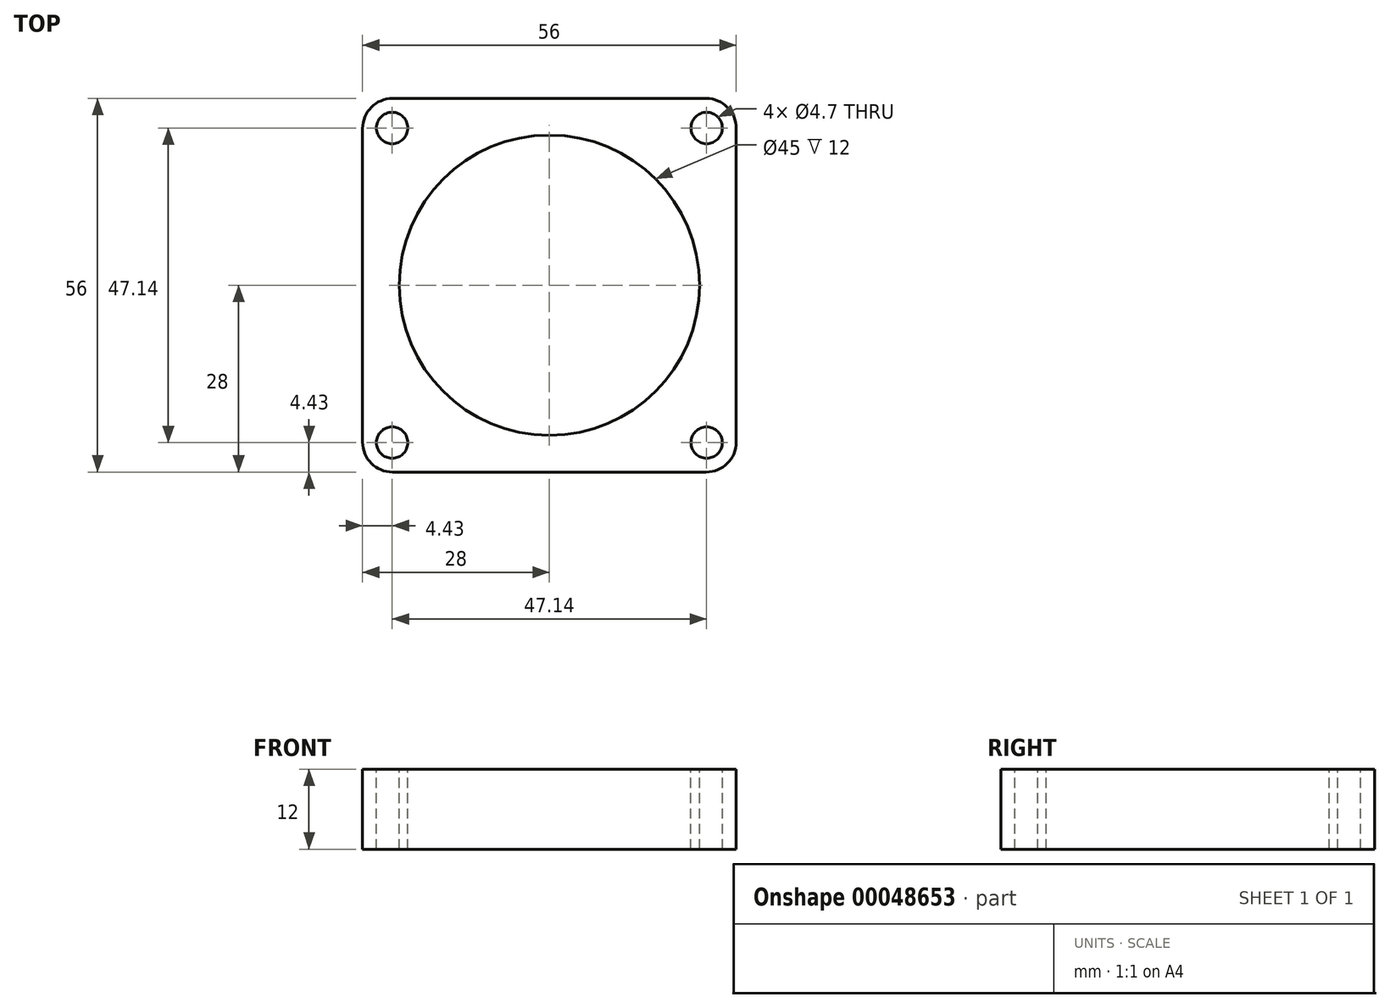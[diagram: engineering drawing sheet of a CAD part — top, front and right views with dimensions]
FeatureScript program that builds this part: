
annotation { "Feature Type Name" : "Feature", "Feature Type Description" : "" }
export const myFeature = defineFeature(function(context is Context, id is Id, definition is map)
    precondition{}
    {
        {
            var Q0;
            Q0=qCreatedBy(makeId("Top.planeOp"),FACE);
            var sketch = newSketch(context, id + "F0", { "sketchPlane" : qUnion([Q0])});
            skLineSegment(sketch, "E0.bottom", {"start": v(0, 0) * mm, "end": v(56, 0) * mm});
            skLineSegment(sketch, "E0.top", {"start": v(0, 56) * mm, "end": v(56, 56) * mm});
            skLineSegment(sketch, "E0.left", {"start": v(0, 0) * mm, "end": v(0, 56) * mm});
            skLineSegment(sketch, "E0.right", {"start": v(56, 0) * mm, "end": v(56, 56) * mm});
            skSolve(sketch);
        }
        {
            var Q0;
            Q0=makeQuery(id+"F0.imprint","IMPRINT",FACE,{"disambiguationData":[TD([[makeQuery(id+"F0.imprint","IMPRINT",EDGE,{"derivedFrom":sQuery(id+"F0.wireOp",EDGE,"E0.bottom")}),1.0]])]});
            extrude(context, id + "F1", {"entities" : qUnion([Q0]), "depth" : 12 * mm});
        }
        {
            var Q0;
            Q0=makeQuery(id+"F1.opExtrude","CAP_FACE",FACE,{"disambiguationData":[OSD([sQuery(id+"F0.wireOp",EDGE,"E0.bottom"),sQuery(id+"F0.wireOp",EDGE,"E0.top"),sQuery(id+"F0.wireOp",EDGE,"E0.left"),sQuery(id+"F0.wireOp",EDGE,"E0.right")])],"isStart":false});
            var sketch = newSketch(context, id + "F2", { "sketchPlane" : qUnion([Q0])});
            skCircle(sketch, "E1", {"center": v(28, 28) * mm, "radius": 22.5 * mm});
            skPoint(sketch, "E2", {"position": v(28, 56) * mm});
            skPoint(sketch, "E3", {"position": v(56, 28) * mm});
            skSolve(sketch);
        }
        {
            var Q0;
            Q0=makeQuery(id+"F2.imprint","IMPRINT",FACE,{"disambiguationData":[TD([[makeQuery(id+"F2.imprint","IMPRINT",EDGE,{"derivedFrom":sQuery(id+"F2.wireOp",EDGE,"E1")}),1.0]])]});
            extrude(context, id + "F3", {"entities" : qUnion([Q0]), "operationType" : NewBodyOperationType.REMOVE, "endBound" : BoundingType.UP_TO_NEXT, "oppositeDirection" : true, "depth" : 25 * mm});
        }
        {
            var Q0;
            Q0=makeQuery(id+"F1.opExtrude","CAP_FACE",FACE,{"disambiguationData":[OSD([sQuery(id+"F0.wireOp",EDGE,"E0.bottom"),sQuery(id+"F0.wireOp",EDGE,"E0.top"),sQuery(id+"F0.wireOp",EDGE,"E0.left"),sQuery(id+"F0.wireOp",EDGE,"E0.right")])],"isStart":false});
            var sketch = newSketch(context, id + "F4", { "sketchPlane" : qUnion([Q0])});
            skLineSegment(sketch, "E4.bottom", {"start": v(4.43, 51.57) * mm, "end": v(51.57, 51.57) * mm});
            skLineSegment(sketch, "E4.top", {"start": v(4.43, 4.43) * mm, "end": v(51.57, 4.43) * mm});
            skLineSegment(sketch, "E4.left", {"start": v(4.43, 51.57) * mm, "end": v(4.43, 4.43) * mm});
            skLineSegment(sketch, "E4.right", {"start": v(51.57, 51.57) * mm, "end": v(51.57, 4.43) * mm});
            skPoint(sketch, "E5", {"position": v(28, 56) * mm});
            skPoint(sketch, "E6", {"position": v(28, 51.57) * mm});
            skPoint(sketch, "E7", {"position": v(51.57, 28) * mm});
            skPoint(sketch, "E8", {"position": v(56, 28) * mm});
            skPoint(sketch, "E9", {"position": v(4.43, 51.57) * mm});
            skPoint(sketch, "E10", {"position": v(51.57, 51.57) * mm});
            skPoint(sketch, "E11", {"position": v(51.57, 4.43) * mm});
            skPoint(sketch, "E12", {"position": v(4.43, 4.43) * mm});
            skSolve(sketch);
        }
        {
            var Q0;
            Q0=sQuery(id+"F4.wireOp",VERTEX,"E9");
            var Q1;
            Q1=sQuery(id+"F4.wireOp",VERTEX,"E10");
            var Q2;
            Q2=sQuery(id+"F4.wireOp",VERTEX,"E11");
            var Q3;
            Q3=sQuery(id+"F4.wireOp",VERTEX,"E12");
            var Q4;
            Q4=makeQuery(id+"F1.opExtrude","SWEPT_BODY",BODY,{"disambiguationData":[OSD([sQuery(id+"F0.wireOp",EDGE,"E0.bottom"),sQuery(id+"F0.wireOp",EDGE,"E0.top"),sQuery(id+"F0.wireOp",EDGE,"E0.left"),sQuery(id+"F0.wireOp",EDGE,"E0.right")])]});
            hole(context, id + "F5", {"style" : HoleStyle.SIMPLE, "holeDiameter" : 4.7 * mm, "endStyle" : HoleEndStyle.THROUGH, "locations" : qUnion([Q0, Q1, Q2, Q3]), "scope" : qUnion([Q4])});
        }
        {
            var Q0;
            Q0=makeQuery(id+"F1.opExtrude","SWEPT_EDGE",EDGE,{"disambiguationData":[OSD([sQuery(id+"F0.wireOp",EDGE,"E0.top"),sQuery(id+"F0.wireOp",EDGE,"E0.right")])]});
            var Q1;
            Q1=makeQuery(id+"F1.opExtrude","SWEPT_EDGE",EDGE,{"disambiguationData":[OSD([sQuery(id+"F0.wireOp",EDGE,"E0.bottom"),sQuery(id+"F0.wireOp",EDGE,"E0.right")])]});
            var Q2;
            Q2=makeQuery(id+"F1.opExtrude","SWEPT_EDGE",EDGE,{"disambiguationData":[OSD([sQuery(id+"F0.wireOp",EDGE,"E0.bottom"),sQuery(id+"F0.wireOp",EDGE,"E0.left")])]});
            var Q3;
            Q3=makeQuery(id+"F1.opExtrude","SWEPT_EDGE",EDGE,{"disambiguationData":[OSD([sQuery(id+"F0.wireOp",EDGE,"E0.top"),sQuery(id+"F0.wireOp",EDGE,"E0.left")])]});
            fillet(context, id + "F6", {"entities" : qUnion([Q0, Q1, Q2, Q3]), "radius" : 4.5 * mm, "tangentPropagation" : true, "allowEdgeOverflow" : false});
        }
    });
